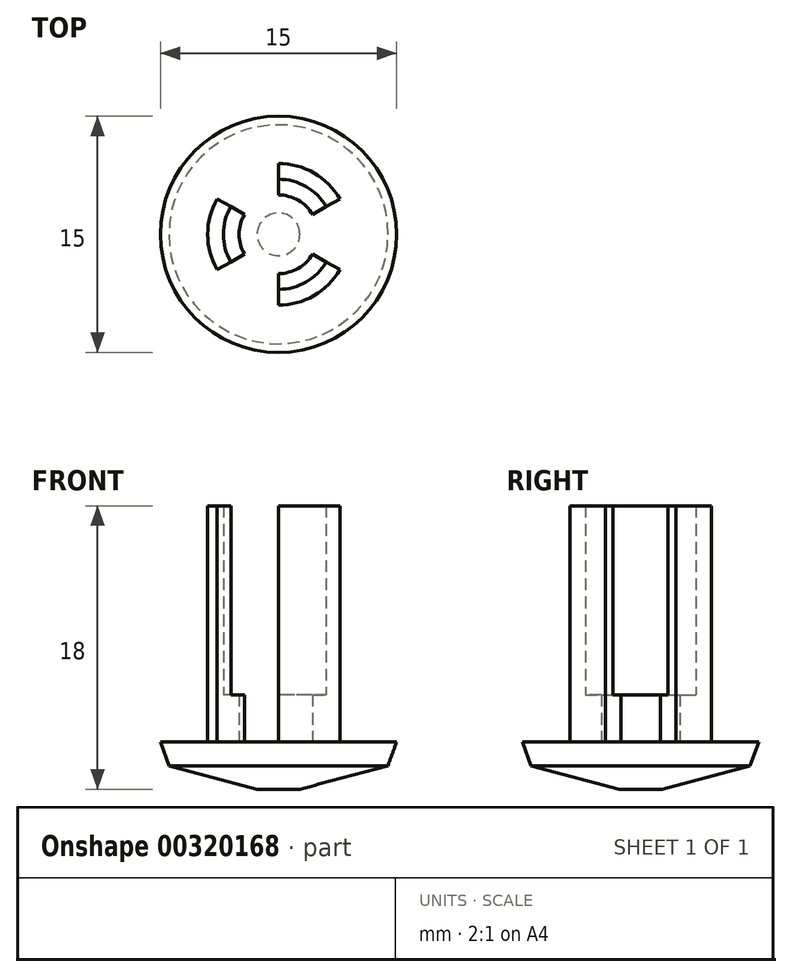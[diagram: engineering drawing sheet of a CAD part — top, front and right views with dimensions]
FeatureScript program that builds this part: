
annotation { "Feature Type Name" : "Feature", "Feature Type Description" : "" }
export const myFeature = defineFeature(function(context is Context, id is Id, definition is map)
    precondition{}
    {
        {
            var Q0;
            Q0=qCreatedBy(makeId("Top.planeOp"),FACE);
            var sketch = newSketch(context, id + "F0", { "sketchPlane" : qUnion([Q0])});
            skCircle(sketch, "E0", {"center": v(0, 0) * mm, "radius": 7.5 * mm});
            skCircle(sketch, "E1", {"center": v(0, 0) * mm, "radius": 3.5 * mm});
            skCircle(sketch, "E2", {"center": v(0, 0) * mm, "radius": 2.5 * mm});
            skLineSegment(sketch, "E3", {"start": v(0, 2.5) * mm, "end": v(0, -2.5) * mm, "construction": true});
            skLineSegment(sketch, "E4", {"start": v(2.17, 1.25) * mm, "end": v(-2.17, -1.25) * mm, "construction": true});
            skLineSegment(sketch, "E5", {"start": v(-2.17, 1.25) * mm, "end": v(2.17, -1.25) * mm, "construction": true});
            skLineSegment(sketch, "E6", {"start": v(0, 2.5) * mm, "end": v(0, 3.5) * mm});
            skLineSegment(sketch, "E7", {"start": v(2.17, 1.25) * mm, "end": v(3.03, 1.75) * mm});
            skLineSegment(sketch, "E8", {"start": v(2.17, -1.25) * mm, "end": v(3.03, -1.75) * mm});
            skLineSegment(sketch, "E9", {"start": v(0, -2.5) * mm, "end": v(0, -3.5) * mm});
            skLineSegment(sketch, "E10", {"start": v(-2.17, -1.25) * mm, "end": v(-3.03, -1.75) * mm});
            skLineSegment(sketch, "E11", {"start": v(-2.17, 1.25) * mm, "end": v(-3.03, 1.75) * mm});
            skCircle(sketch, "E12", {"center": v(0, 0) * mm, "radius": 4.5 * mm});
            skLineSegment(sketch, "E13", {"start": v(0, 3.5) * mm, "end": v(0, 4.5) * mm});
            skLineSegment(sketch, "E14", {"start": v(3.03, 1.75) * mm, "end": v(3.9, 2.25) * mm});
            skLineSegment(sketch, "E15", {"start": v(3.03, -1.75) * mm, "end": v(3.9, -2.25) * mm});
            skLineSegment(sketch, "E16", {"start": v(0, -3.5) * mm, "end": v(0, -4.5) * mm});
            skLineSegment(sketch, "E17", {"start": v(-3.03, -1.75) * mm, "end": v(-3.9, -2.25) * mm});
            skLineSegment(sketch, "E18", {"start": v(-3.03, 1.75) * mm, "end": v(-3.9, 2.25) * mm});
            skSolve(sketch);
        }
        {
            var Q0;
            Q0=makeQuery(id+"F0.imprint","IMPRINT",FACE,{"disambiguationData":[TD([[makeQuery(id+"F0.imprint","IMPRINT",EDGE,{"derivedFrom":sQuery(id+"F0.wireOp",EDGE,"E0")}),1.0]])]});
            var Q1;
            {var subQ0=sQuery(id+"F0.wireOp",EDGE,"E15");Q1=makeQuery(id+"F0.imprint","IMPRINT",FACE,{"disambiguationData":[TD([[makeQuery(id+"F0.imprint","IMPRINT",EDGE,{"derivedFrom":subQ0}),-1.0]])]});}
            var Q2;
            {var subQ0=sQuery(id+"F0.wireOp",EDGE,"E8");Q2=makeQuery(id+"F0.imprint","IMPRINT",FACE,{"disambiguationData":[TD([[makeQuery(id+"F0.imprint","IMPRINT",EDGE,{"derivedFrom":subQ0}),-1.0]])]});}
            var Q3;
            {var subQ0=sQuery(id+"F0.wireOp",EDGE,"E9");Q3=makeQuery(id+"F0.imprint","IMPRINT",FACE,{"disambiguationData":[TD([[makeQuery(id+"F0.imprint","IMPRINT",EDGE,{"derivedFrom":subQ0}),-1.0]])]});}
            var Q4;
            {var subQ0=sQuery(id+"F0.wireOp",EDGE,"E16");Q4=makeQuery(id+"F0.imprint","IMPRINT",FACE,{"disambiguationData":[TD([[makeQuery(id+"F0.imprint","IMPRINT",EDGE,{"derivedFrom":subQ0}),-1.0]])]});}
            var Q5;
            {var subQ0=sQuery(id+"F0.wireOp",EDGE,"E17");Q5=makeQuery(id+"F0.imprint","IMPRINT",FACE,{"disambiguationData":[TD([[makeQuery(id+"F0.imprint","IMPRINT",EDGE,{"derivedFrom":subQ0}),-1.0]])]});}
            var Q6;
            {var subQ0=sQuery(id+"F0.wireOp",EDGE,"E10");Q6=makeQuery(id+"F0.imprint","IMPRINT",FACE,{"disambiguationData":[TD([[makeQuery(id+"F0.imprint","IMPRINT",EDGE,{"derivedFrom":subQ0}),-1.0]])]});}
            var Q7;
            {var subQ0=sQuery(id+"F0.wireOp",EDGE,"E13");Q7=makeQuery(id+"F0.imprint","IMPRINT",FACE,{"disambiguationData":[TD([[makeQuery(id+"F0.imprint","IMPRINT",EDGE,{"derivedFrom":subQ0}),1.0]])]});}
            var Q8;
            {var subQ0=sQuery(id+"F0.wireOp",EDGE,"E6");Q8=makeQuery(id+"F0.imprint","IMPRINT",FACE,{"disambiguationData":[TD([[makeQuery(id+"F0.imprint","IMPRINT",EDGE,{"derivedFrom":subQ0}),1.0]])]});}
            var Q9;
            {var subQ0=sQuery(id+"F0.wireOp",EDGE,"E13");Q9=makeQuery(id+"F0.imprint","IMPRINT",FACE,{"disambiguationData":[TD([[makeQuery(id+"F0.imprint","IMPRINT",EDGE,{"derivedFrom":subQ0}),-1.0]])]});}
            var Q10;
            {var subQ0=sQuery(id+"F0.wireOp",EDGE,"E6");Q10=makeQuery(id+"F0.imprint","IMPRINT",FACE,{"disambiguationData":[TD([[makeQuery(id+"F0.imprint","IMPRINT",EDGE,{"derivedFrom":subQ0}),-1.0]])]});}
            var Q11;
            {var subQ0=sQuery(id+"F0.wireOp",EDGE,"E14");Q11=makeQuery(id+"F0.imprint","IMPRINT",FACE,{"disambiguationData":[TD([[makeQuery(id+"F0.imprint","IMPRINT",EDGE,{"derivedFrom":subQ0}),-1.0]])]});}
            var Q12;
            {var subQ0=sQuery(id+"F0.wireOp",EDGE,"E7");Q12=makeQuery(id+"F0.imprint","IMPRINT",FACE,{"disambiguationData":[TD([[makeQuery(id+"F0.imprint","IMPRINT",EDGE,{"derivedFrom":subQ0}),-1.0]])]});}
            var Q13;
            {var subQ0=sQuery(id+"F0.wireOp",EDGE,"E2");var subQ4=makeQuery(id+"F0.imprint","INTERSECT",VERTEX,{"derivedFrom":[subQ0,sQuery(id+"F0.wireOp",EDGE,"E6")]});Q13=makeQuery(id+"F0.imprint","IMPRINT",FACE,{"disambiguationData":[TD([[makeQuery(id+"F0.imprint","IMPRINT",EDGE,{"disambiguationData":[TD([[subQ4,1.0]])],"derivedFrom":subQ0}),1.0]])]});}
            extrude(context, id + "F1", {"entities" : qUnion([Q0, Q1, Q2, Q3, Q4, Q5, Q6, Q7, Q8, Q9, Q10, Q11, Q12, Q13]), "oppositeDirection" : true, "depth" : 1.5 * mm, "hasDraft" : true, "draftAngle" : 20 * degree, "draftPullDirection" : true});
        }
        {
            var Q0;
            {var subQ0=sQuery(id+"F0.wireOp",EDGE,"E6");Q0=makeQuery(id+"F0.imprint","IMPRINT",FACE,{"disambiguationData":[TD([[makeQuery(id+"F0.imprint","IMPRINT",EDGE,{"derivedFrom":subQ0}),-1.0]])]});}
            var Q1;
            {var subQ0=sQuery(id+"F0.wireOp",EDGE,"E8");Q1=makeQuery(id+"F0.imprint","IMPRINT",FACE,{"disambiguationData":[TD([[makeQuery(id+"F0.imprint","IMPRINT",EDGE,{"derivedFrom":subQ0}),-1.0]])]});}
            var Q2;
            {var subQ0=sQuery(id+"F0.wireOp",EDGE,"E10");Q2=makeQuery(id+"F0.imprint","IMPRINT",FACE,{"disambiguationData":[TD([[makeQuery(id+"F0.imprint","IMPRINT",EDGE,{"derivedFrom":subQ0}),-1.0]])]});}
            extrude(context, id + "F2", {"entities" : qUnion([Q0, Q1, Q2]), "operationType" : NewBodyOperationType.ADD, "depth" : 3 * mm});
        }
        {
            var Q0;
            {var subQ0=sQuery(id+"F0.wireOp",EDGE,"E17");Q0=makeQuery(id+"F0.imprint","IMPRINT",FACE,{"disambiguationData":[TD([[makeQuery(id+"F0.imprint","IMPRINT",EDGE,{"derivedFrom":subQ0}),-1.0]])]});}
            var Q1;
            {var subQ0=sQuery(id+"F0.wireOp",EDGE,"E15");Q1=makeQuery(id+"F0.imprint","IMPRINT",FACE,{"disambiguationData":[TD([[makeQuery(id+"F0.imprint","IMPRINT",EDGE,{"derivedFrom":subQ0}),-1.0]])]});}
            var Q2;
            {var subQ0=sQuery(id+"F0.wireOp",EDGE,"E13");Q2=makeQuery(id+"F0.imprint","IMPRINT",FACE,{"disambiguationData":[TD([[makeQuery(id+"F0.imprint","IMPRINT",EDGE,{"derivedFrom":subQ0}),-1.0]])]});}
            extrude(context, id + "F3", {"entities" : qUnion([Q0, Q1, Q2]), "operationType" : NewBodyOperationType.ADD, "depth" : 15 * mm});
        }
        {
            var Q0;
            Q0=makeQuery(id+"F1.opExtrude","CAP_FACE",FACE,{"disambiguationData":[OSD([sQuery(id+"F0.wireOp",EDGE,"E0")])],"isStart":false});
            extrude(context, id + "F4", {"entities" : qUnion([Q0]), "depth" : 1.5 * mm, "hasDraft" : true, "draftAngle" : 75 * degree, "draftPullDirection" : true});
        }
    });
